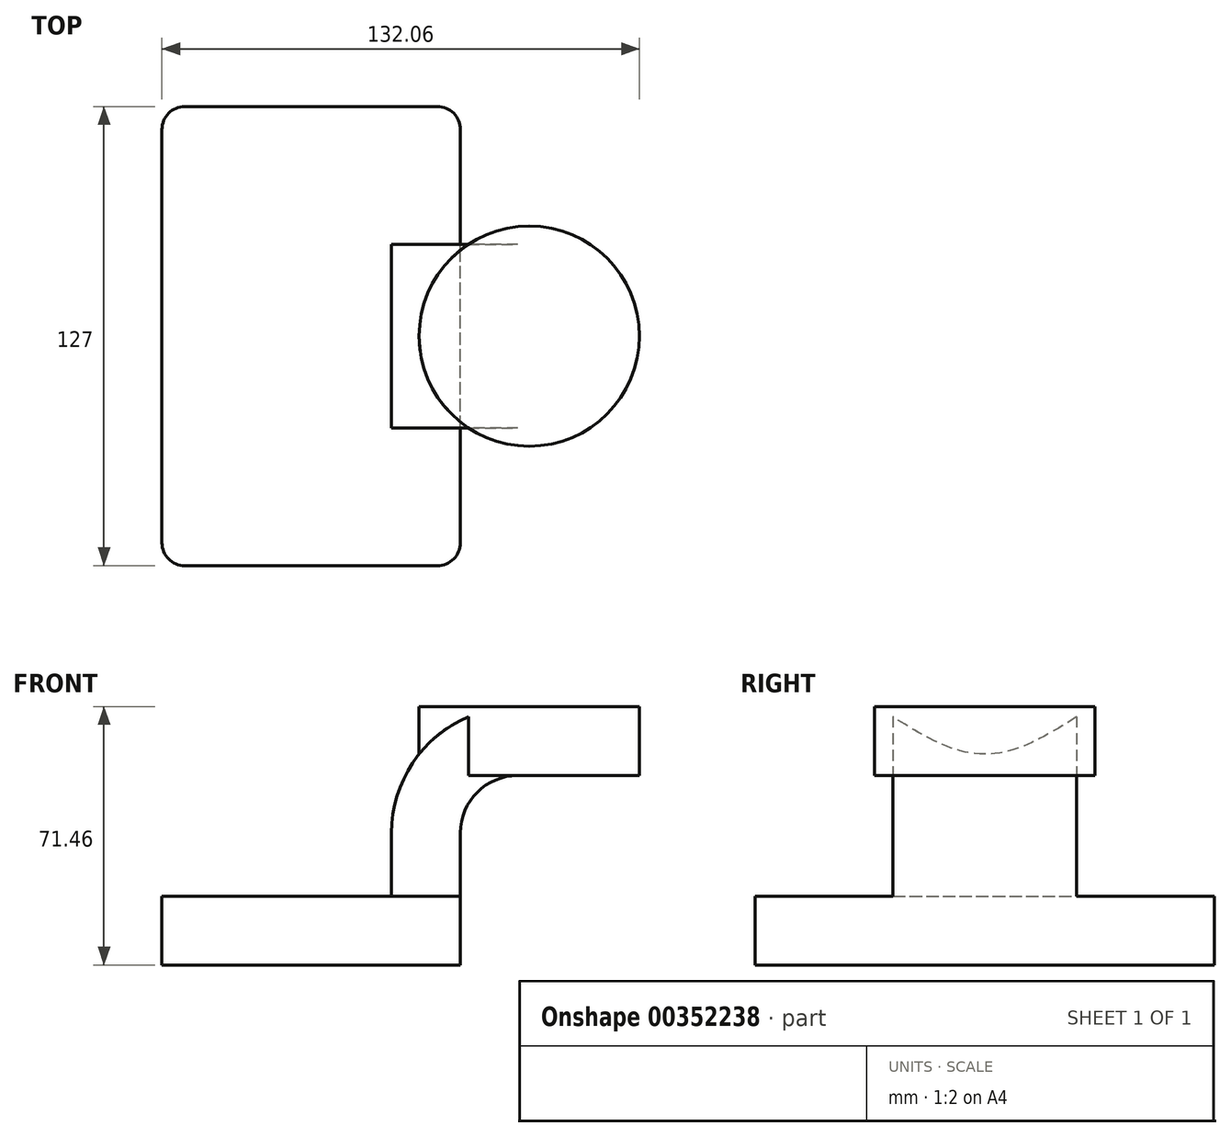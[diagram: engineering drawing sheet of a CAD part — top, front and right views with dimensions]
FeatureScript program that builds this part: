
annotation { "Feature Type Name" : "Feature", "Feature Type Description" : "" }
export const myFeature = defineFeature(function(context is Context, id is Id, definition is map)
    precondition{}
    {
        {
            var Q0;
            Q0=qCreatedBy(makeId("Front.planeOp"),FACE);
            var sketch = newSketch(context, id + "F0", { "sketchPlane" : qUnion([Q0])});
            skLineSegment(sketch, "E0.bottom", {"start": v(-41.28, -9.53) * mm, "end": v(41.28, -9.53) * mm});
            skLineSegment(sketch, "E0.top", {"start": v(-41.28, 9.53) * mm, "end": v(41.28, 9.53) * mm});
            skLineSegment(sketch, "E0.left", {"start": v(-41.28, -9.53) * mm, "end": v(-41.28, 9.53) * mm});
            skLineSegment(sketch, "E0.right", {"start": v(41.28, -9.53) * mm, "end": v(41.28, 9.52) * mm});
            skPoint(sketch, "E0.middle", {"position": v(0, 0) * mm});
            skLineSegment(sketch, "E1.bottom", {"start": v(60.33, 38.1) * mm, "end": v(111.12, 38.1) * mm});
            skLineSegment(sketch, "E1.top", {"start": v(60.33, 66.67) * mm, "end": v(111.12, 66.67) * mm});
            skLineSegment(sketch, "E1.left", {"start": v(60.33, 38.1) * mm, "end": v(60.33, 66.67) * mm});
            skLineSegment(sketch, "E1.right", {"start": v(111.12, 38.1) * mm, "end": v(111.12, 66.67) * mm});
            skPoint(sketch, "E1.middle", {"position": v(85.72, 52.39) * mm});
            skLineSegment(sketch, "E2", {"start": v(41.28, 9.52) * mm, "end": v(41.28, 27) * mm});
            skArc(sketch, "E3", {"start": v(41.27, 27) * mm, "mid": v(45.92, 38.23) * mm, "end": v(57.15, 42.88) * mm});
            skLineSegment(sketch, "E4", {"start": v(57.15, 42.88) * mm, "end": v(91.27, 42.88) * mm});
            skLineSegment(sketch, "E5.0", {"start": v(57.15, 61.93) * mm, "end": v(91.27, 61.93) * mm});
            skArc(sketch, "E5.1", {"start": v(22.22, 27) * mm, "mid": v(32.45, 51.7) * mm, "end": v(57.15, 61.93) * mm});
            skLineSegment(sketch, "E5.2", {"start": v(22.22, 9.52) * mm, "end": v(22.22, 27) * mm});
            skLineSegment(sketch, "E6", {"start": v(90.8, 66.67) * mm, "end": v(90.8, 38.1) * mm});
            skFitSpline(sketch, "E7", {"points": [v(-41.28, 9.52) * mm, v(60.33, 61.93) * mm], "startDerivative": vector(29.94, 118.62) * mm, "endDerivative": vector(203, -0.83) * mm});
            skSolve(sketch);
        }
        {
            var Q0;
            Q0=makeQuery(id+"F0.imprint","IMPRINT",FACE,{"disambiguationData":[TD([[makeQuery(id+"F0.imprint","IMPRINT",EDGE,{"derivedFrom":sQuery(id+"F0.wireOp",EDGE,"E0.bottom")}),1.0]])]});
            extrude(context, id + "F1", {"entities" : qUnion([Q0]), "endBound" : BoundingType.SYMMETRIC, "depth" : 127 * mm});
        }
        {
            var Q0;
            {var subQ1=sQuery(id+"F0.wireOp",EDGE,"E5.1");Q0=makeQuery(id+"F0.imprint","IMPRINT",FACE,{"disambiguationData":[TD([[makeQuery(id+"F0.imprint","IMPRINT",EDGE,{"derivedFrom":subQ1}),1.0]])]});}
            extrude(context, id + "F2", {"entities" : qUnion([Q0]), "operationType" : NewBodyOperationType.ADD, "endBound" : BoundingType.SYMMETRIC, "depth" : 15.88 * mm});
        }
        {
            var Q0;
            {var subQ1=sQuery(id+"F0.wireOp",EDGE,"E2");Q0=makeQuery(id+"F0.imprint","IMPRINT",FACE,{"disambiguationData":[TD([[makeQuery(id+"F0.imprint","IMPRINT",EDGE,{"derivedFrom":subQ1}),1.0]])]});}
            extrude(context, id + "F3", {"entities" : qUnion([Q0]), "operationType" : NewBodyOperationType.ADD, "endBound" : BoundingType.SYMMETRIC, "depth" : 50.8 * mm});
        }
        {
            var Q0;
            {var subQ1=sQuery(id+"F0.wireOp",EDGE,"E1.left");var subQ3=sQuery(id+"F0.wireOp",EDGE,"E4");var subQ4=makeQuery(id+"F0.imprint","INTERSECT",VERTEX,{"derivedFrom":[subQ1,subQ3]});Q0=makeQuery(id+"F0.imprint","IMPRINT",FACE,{"disambiguationData":[TD([[makeQuery(id+"F0.imprint","IMPRINT",EDGE,{"disambiguationData":[TD([[subQ4,-1.0]])],"derivedFrom":subQ3}),1.0]])]});}
            var Q1;
            Q1=sQuery(id+"F0.wireOp",EDGE,"E1.left");
            revolve(context, id + "F4", {"operationType" : NewBodyOperationType.ADD, "entities" : qUnion([Q0]), "axis" : qUnion([Q1]), "revolveType" : RevolveType.FULL});
        }
        {
            var Q0;
            Q0=makeQuery(id+"F1.opExtrude","CAP_EDGE",EDGE,{"disambiguationData":[OSD([sQuery(id+"F0.wireOp",EDGE,"E0.right")])],"isStart":false});
            var Q1;
            Q1=makeQuery(id+"F1.opExtrude","CAP_EDGE",EDGE,{"disambiguationData":[OSD([sQuery(id+"F0.wireOp",EDGE,"E0.left")])],"isStart":false});
            var Q2;
            Q2=makeQuery(id+"F1.opExtrude","CAP_EDGE",EDGE,{"disambiguationData":[OSD([sQuery(id+"F0.wireOp",EDGE,"E0.left")])],"isStart":true});
            var Q3;
            Q3=makeQuery(id+"F1.opExtrude","CAP_EDGE",EDGE,{"disambiguationData":[OSD([sQuery(id+"F0.wireOp",EDGE,"E0.right")])],"isStart":true});
            fillet(context, id + "F5", {"entities" : qUnion([Q0, Q1, Q2, Q3]), "radius" : 6.35 * mm, "tangentPropagation" : true, "allowEdgeOverflow" : false});
        }
    });
